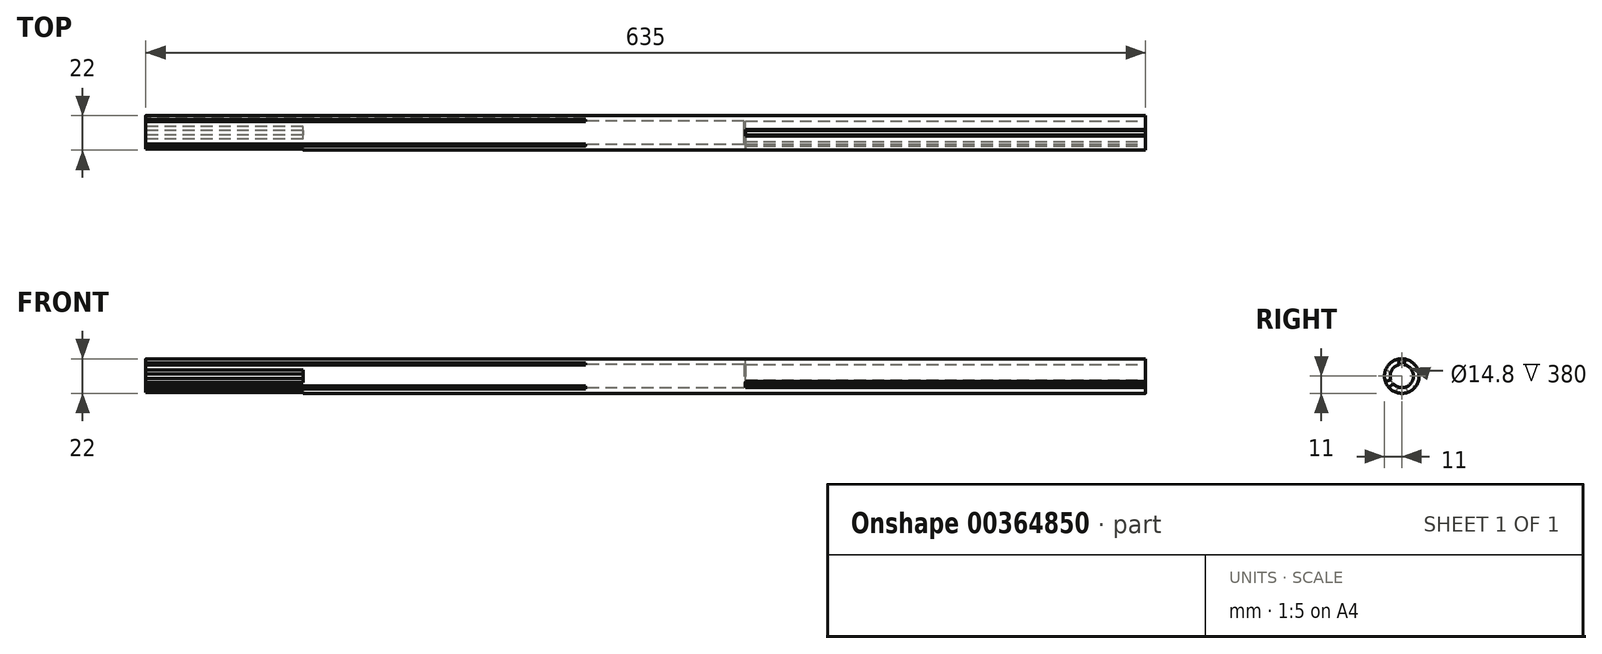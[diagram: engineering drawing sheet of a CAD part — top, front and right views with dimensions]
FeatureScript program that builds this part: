
annotation { "Feature Type Name" : "Feature", "Feature Type Description" : "" }
export const myFeature = defineFeature(function(context is Context, id is Id, definition is map)
    precondition{}
    {
        {
            var Q0;
            Q0=qCreatedBy(makeId("Right.planeOp"),FACE);
            var sketch = newSketch(context, id + "F0", { "sketchPlane" : qUnion([Q0])});
            skCircle(sketch, "E0", {"center": v(0, 0) * mm, "radius": 11 * mm});
            skSolve(sketch);
        }
        {
            var Q0;
            Q0=makeQuery(id+"F0.imprint","IMPRINT",FACE,{"disambiguationData":[TD([[makeQuery(id+"F0.imprint","IMPRINT",EDGE,{"derivedFrom":sQuery(id+"F0.wireOp",EDGE,"E0")}),1.0]])]});
            extrude(context, id + "F1", {"entities" : qUnion([Q0]), "depth" : 635 * mm});
        }
        {
            var Q0;
            Q0=makeQuery(id+"F1.opExtrude","CAP_FACE",FACE,{"disambiguationData":[OSD([sQuery(id+"F0.wireOp",EDGE,"E0")])],"isStart":false});
            var sketch = newSketch(context, id + "F2", { "sketchPlane" : qUnion([Q0])});
            skCircle(sketch, "E1", {"center": v(0, 0) * mm, "radius": 7.39 * mm});
            skLineSegment(sketch, "E2", {"start": v(0, 0) * mm, "end": v(-10.42, -3.54) * mm});
            skLineSegment(sketch, "E3", {"start": v(0, 0) * mm, "end": v(2.15, 10.79) * mm});
            skLineSegment(sketch, "E4", {"start": v(0, 0) * mm, "end": v(8.27, -7.25) * mm});
            skLineSegment(sketch, "E5", {"start": v(-8.27, -7.25) * mm, "end": v(0, 0) * mm});
            skLineSegment(sketch, "E6", {"start": v(0, 0) * mm, "end": v(10.42, -3.54) * mm});
            skLineSegment(sketch, "E7", {"start": v(0, 0) * mm, "end": v(-2.15, 10.79) * mm});
            skLineSegment(sketch, "E8", {"start": v(0, 0) * mm, "end": v(0, 7.39) * mm});
            skSolve(sketch);
        }
        {
            var Q0;
            {var subQ3=sQuery(id+"F2.wireOp",EDGE,"E1");var subQ5=makeQuery(id+"F2.imprint","INTERSECT",VERTEX,{"derivedFrom":[subQ3,sQuery(id+"F2.wireOp",EDGE,"E8")]});Q0=makeQuery(id+"F2.imprint","IMPRINT",FACE,{"disambiguationData":[TD([[makeQuery(id+"F2.imprint","IMPRINT",EDGE,{"disambiguationData":[TD([[subQ5,1.0]])],"derivedFrom":subQ3}),-1.0]])]});}
            var Q1;
            {var subQ0=sQuery(id+"F2.wireOp",EDGE,"E7");var subQ1=sQuery(id+"F2.wireOp",EDGE,"E1");var subQ2=makeQuery(id+"F2.imprint","INTERSECT",VERTEX,{"derivedFrom":[subQ1,subQ0]});Q1=makeQuery(id+"F2.imprint","IMPRINT",FACE,{"disambiguationData":[TD([[makeQuery(id+"F2.imprint","IMPRINT",EDGE,{"disambiguationData":[TD([[subQ2,-1.0]])],"derivedFrom":subQ1}),1.0]])]});}
            var Q2;
            {var subQ0=sQuery(id+"F2.wireOp",EDGE,"E2");var subQ1=sQuery(id+"F2.wireOp",EDGE,"E1");var subQ2=makeQuery(id+"F2.imprint","INTERSECT",VERTEX,{"derivedFrom":[subQ1,subQ0]});Q2=makeQuery(id+"F2.imprint","IMPRINT",FACE,{"disambiguationData":[TD([[makeQuery(id+"F2.imprint","IMPRINT",EDGE,{"disambiguationData":[TD([[subQ2,-1.0]])],"derivedFrom":subQ1}),1.0]])]});}
            var Q3;
            {var subQ0=sQuery(id+"F2.wireOp",EDGE,"E5");var subQ1=sQuery(id+"F2.wireOp",EDGE,"E1");var subQ2=makeQuery(id+"F2.imprint","INTERSECT",VERTEX,{"derivedFrom":[subQ1,subQ0]});Q3=makeQuery(id+"F2.imprint","IMPRINT",FACE,{"disambiguationData":[TD([[makeQuery(id+"F2.imprint","IMPRINT",EDGE,{"disambiguationData":[TD([[subQ2,-1.0]])],"derivedFrom":subQ1}),1.0]])]});}
            var Q4;
            {var subQ0=sQuery(id+"F2.wireOp",EDGE,"E4");var subQ1=sQuery(id+"F2.wireOp",EDGE,"E1");var subQ2=makeQuery(id+"F2.imprint","INTERSECT",VERTEX,{"derivedFrom":[subQ1,subQ0]});Q4=makeQuery(id+"F2.imprint","IMPRINT",FACE,{"disambiguationData":[TD([[makeQuery(id+"F2.imprint","IMPRINT",EDGE,{"disambiguationData":[TD([[subQ2,-1.0]])],"derivedFrom":subQ1}),1.0]])]});}
            var Q5;
            {var subQ0=sQuery(id+"F2.wireOp",EDGE,"E3");var subQ1=sQuery(id+"F2.wireOp",EDGE,"E1");var subQ2=makeQuery(id+"F2.imprint","INTERSECT",VERTEX,{"derivedFrom":[subQ1,subQ0]});Q5=makeQuery(id+"F2.imprint","IMPRINT",FACE,{"disambiguationData":[TD([[makeQuery(id+"F2.imprint","IMPRINT",EDGE,{"disambiguationData":[TD([[subQ2,1.0]])],"derivedFrom":subQ1}),1.0]])]});}
            var Q6;
            {var subQ0=sQuery(id+"F2.wireOp",EDGE,"E8");Q6=makeQuery(id+"F2.imprint","IMPRINT",FACE,{"disambiguationData":[TD([[makeQuery(id+"F2.imprint","IMPRINT",EDGE,{"derivedFrom":subQ0}),-1.0]])]});}
            var Q7;
            {var subQ0=sQuery(id+"F2.wireOp",EDGE,"E8");Q7=makeQuery(id+"F2.imprint","IMPRINT",FACE,{"disambiguationData":[TD([[makeQuery(id+"F2.imprint","IMPRINT",EDGE,{"derivedFrom":subQ0}),1.0]])]});}
            var Q8;
            {var subQ0=sQuery(id+"F2.wireOp",EDGE,"E2");var subQ1=sQuery(id+"F2.wireOp",EDGE,"E1");var subQ2=makeQuery(id+"F2.imprint","INTERSECT",VERTEX,{"derivedFrom":[subQ1,subQ0]});Q8=makeQuery(id+"F2.imprint","IMPRINT",FACE,{"disambiguationData":[TD([[makeQuery(id+"F2.imprint","IMPRINT",EDGE,{"disambiguationData":[TD([[subQ2,-1.0]])],"derivedFrom":subQ1}),-1.0]])]});}
            var Q9;
            {var subQ0=sQuery(id+"F2.wireOp",EDGE,"E4");var subQ1=sQuery(id+"F2.wireOp",EDGE,"E1");var subQ2=makeQuery(id+"F2.imprint","INTERSECT",VERTEX,{"derivedFrom":[subQ1,subQ0]});Q9=makeQuery(id+"F2.imprint","IMPRINT",FACE,{"disambiguationData":[TD([[makeQuery(id+"F2.imprint","IMPRINT",EDGE,{"disambiguationData":[TD([[subQ2,-1.0]])],"derivedFrom":subQ1}),-1.0]])]});}
            extrude(context, id + "F3", {"entities" : qUnion([Q0, Q1, Q2, Q3, Q4, Q5, Q6, Q7, Q8, Q9]), "operationType" : NewBodyOperationType.REMOVE, "oppositeDirection" : true, "depth" : 254 * mm});
        }
        {
            var Q0;
            Q0=makeQuery(id+"F1.opExtrude","CAP_FACE",FACE,{"disambiguationData":[OSD([sQuery(id+"F0.wireOp",EDGE,"E0")])],"isStart":true});
            var sketch = newSketch(context, id + "F4", { "sketchPlane" : qUnion([Q0])});
            skCircle(sketch, "E9", {"center": v(0, 0) * mm, "radius": 7.4 * mm});
            skSolve(sketch);
        }
        {
            var Q0;
            Q0=makeQuery(id+"F4.imprint","IMPRINT",FACE,{"disambiguationData":[TD([[makeQuery(id+"F4.imprint","IMPRINT",EDGE,{"derivedFrom":sQuery(id+"F4.wireOp",EDGE,"E9")}),1.0]])]});
            extrude(context, id + "F5", {"entities" : qUnion([Q0]), "operationType" : NewBodyOperationType.REMOVE, "oppositeDirection" : true, "depth" : 380 * mm});
        }
        {
            var Q0;
            Q0=makeQuery(id+"F1.opExtrude","CAP_FACE",FACE,{"disambiguationData":[OSD([sQuery(id+"F0.wireOp",EDGE,"E0")])],"isStart":true});
            var sketch = newSketch(context, id + "F6", { "sketchPlane" : qUnion([Q0])});
            skLineSegment(sketch, "E10.bottom", {"start": v(7.12, 6.97) * mm, "end": v(9.12, 6.97) * mm});
            skLineSegment(sketch, "E10.top", {"start": v(7.12, 8.97) * mm, "end": v(9.12, 8.97) * mm});
            skLineSegment(sketch, "E10.left", {"start": v(7.12, 6.97) * mm, "end": v(7.12, 8.97) * mm});
            skLineSegment(sketch, "E10.right", {"start": v(9.12, 6.97) * mm, "end": v(9.12, 8.97) * mm});
            skLineSegment(sketch, "E11.bottom", {"start": v(-7.2, 6.97) * mm, "end": v(-9.2, 6.97) * mm});
            skLineSegment(sketch, "E11.top", {"start": v(-7.2, 8.97) * mm, "end": v(-9.2, 8.97) * mm});
            skLineSegment(sketch, "E11.left", {"start": v(-7.2, 6.97) * mm, "end": v(-7.2, 8.97) * mm});
            skLineSegment(sketch, "E11.right", {"start": v(-9.2, 6.97) * mm, "end": v(-9.2, 8.97) * mm});
            skLineSegment(sketch, "E12.bottom", {"start": v(-7.2, -6.27) * mm, "end": v(-9.2, -6.27) * mm});
            skLineSegment(sketch, "E12.top", {"start": v(-7.2, -8.27) * mm, "end": v(-9.2, -8.27) * mm});
            skLineSegment(sketch, "E12.left", {"start": v(-7.2, -6.27) * mm, "end": v(-7.2, -8.27) * mm});
            skLineSegment(sketch, "E12.right", {"start": v(-9.2, -6.27) * mm, "end": v(-9.2, -8.27) * mm});
            skLineSegment(sketch, "E13.bottom", {"start": v(7.12, -6.27) * mm, "end": v(9.12, -6.27) * mm});
            skLineSegment(sketch, "E13.top", {"start": v(7.12, -8.27) * mm, "end": v(9.12, -8.27) * mm});
            skLineSegment(sketch, "E13.left", {"start": v(7.12, -6.27) * mm, "end": v(7.12, -8.27) * mm});
            skLineSegment(sketch, "E13.right", {"start": v(9.12, -6.27) * mm, "end": v(9.12, -8.27) * mm});
            skCircle(sketch, "E14", {"center": v(11, 0) * mm, "radius": 4 * mm});
            skCircle(sketch, "E15", {"center": v(0, 11) * mm, "radius": 4 * mm});
            skCircle(sketch, "E16", {"center": v(-11, 0) * mm, "radius": 4 * mm});
            skCircle(sketch, "E17", {"center": v(0, -11) * mm, "radius": 4 * mm});
            skSolve(sketch);
        }
        {
            var Q0;
            {var subQ0=sQuery(id+"F6.wireOp",EDGE,"E10.left");var subQ1=sQuery(id+"F6.wireOp",EDGE,"E10.bottom");var subQ2=makeQuery(id+"F6.imprint","INTERSECT",VERTEX,{"derivedFrom":[subQ1,subQ0]});Q0=makeQuery(id+"F6.imprint","IMPRINT",FACE,{"disambiguationData":[TD([[makeQuery(id+"F6.imprint","IMPRINT",EDGE,{"disambiguationData":[TD([[subQ2,-1.0]])],"derivedFrom":subQ1}),1.0]])]});}
            var Q1;
            {var subQ0=sQuery(id+"F6.wireOp",EDGE,"E12.left");Q1=makeQuery(id+"F6.imprint","IMPRINT",FACE,{"disambiguationData":[TD([[makeQuery(id+"F6.imprint","IMPRINT",EDGE,{"derivedFrom":subQ0}),-1.0]])]});}
            var Q2;
            {var subQ0=sQuery(id+"F6.wireOp",EDGE,"E13.left");Q2=makeQuery(id+"F6.imprint","IMPRINT",FACE,{"disambiguationData":[TD([[makeQuery(id+"F6.imprint","IMPRINT",EDGE,{"derivedFrom":subQ0}),1.0]])]});}
            var Q3;
            {var subQ0=sQuery(id+"F6.wireOp",EDGE,"E11.left");var subQ1=sQuery(id+"F6.wireOp",EDGE,"E11.bottom");var subQ2=makeQuery(id+"F6.imprint","INTERSECT",VERTEX,{"derivedFrom":[subQ1,subQ0]});Q3=makeQuery(id+"F6.imprint","IMPRINT",FACE,{"disambiguationData":[TD([[makeQuery(id+"F6.imprint","IMPRINT",EDGE,{"disambiguationData":[TD([[subQ2,-1.0]])],"derivedFrom":subQ1}),-1.0]])]});}
            extrude(context, id + "F7", {"entities" : qUnion([Q0, Q1, Q2, Q3]), "operationType" : NewBodyOperationType.REMOVE, "oppositeDirection" : true, "depth" : 279.4 * mm});
        }
        {
            var Q0;
            {var subQ0=sQuery(id+"F6.wireOp",EDGE,"E14");var subQ1=makeQuery(id+"F1.opExtrude","CAP_EDGE",EDGE,{"disambiguationData":[OSD([sQuery(id+"F0.wireOp",EDGE,"E0")])],"isStart":true});var subQ2=makeQuery(id+"F6.imprint","INTERSECT",VERTEX,{"disambiguationData":[OD(0.0)],"derivedFrom":[subQ1,subQ0]});Q0=makeQuery(id+"F6.imprint","IMPRINT",FACE,{"disambiguationData":[TD([[makeQuery(id+"F6.imprint","IMPRINT",EDGE,{"disambiguationData":[TD([[subQ2,-1.0]])],"derivedFrom":subQ0}),1.0]])]});}
            var Q1;
            {var subQ0=sQuery(id+"F6.wireOp",EDGE,"E17");var subQ1=makeQuery(id+"F1.opExtrude","CAP_EDGE",EDGE,{"disambiguationData":[OSD([sQuery(id+"F0.wireOp",EDGE,"E0")])],"isStart":true});var subQ2=makeQuery(id+"F6.imprint","INTERSECT",VERTEX,{"disambiguationData":[OD(0.0)],"derivedFrom":[subQ1,subQ0]});Q1=makeQuery(id+"F6.imprint","IMPRINT",FACE,{"disambiguationData":[TD([[makeQuery(id+"F6.imprint","IMPRINT",EDGE,{"disambiguationData":[TD([[subQ2,1.0]])],"derivedFrom":subQ0}),1.0]])]});}
            var Q2;
            {var subQ0=sQuery(id+"F6.wireOp",EDGE,"E16");var subQ1=makeQuery(id+"F1.opExtrude","CAP_EDGE",EDGE,{"disambiguationData":[OSD([sQuery(id+"F0.wireOp",EDGE,"E0")])],"isStart":true});var subQ2=makeQuery(id+"F6.imprint","INTERSECT",VERTEX,{"disambiguationData":[OD(0.0)],"derivedFrom":[subQ1,subQ0]});Q2=makeQuery(id+"F6.imprint","IMPRINT",FACE,{"disambiguationData":[TD([[makeQuery(id+"F6.imprint","IMPRINT",EDGE,{"disambiguationData":[TD([[subQ2,1.0]])],"derivedFrom":subQ0}),1.0]])]});}
            var Q3;
            {var subQ0=sQuery(id+"F6.wireOp",EDGE,"E15");var subQ1=makeQuery(id+"F1.opExtrude","CAP_EDGE",EDGE,{"disambiguationData":[OSD([sQuery(id+"F0.wireOp",EDGE,"E0")])],"isStart":true});var subQ2=makeQuery(id+"F6.imprint","INTERSECT",VERTEX,{"disambiguationData":[OD(0.0)],"derivedFrom":[subQ1,subQ0]});Q3=makeQuery(id+"F6.imprint","IMPRINT",FACE,{"disambiguationData":[TD([[makeQuery(id+"F6.imprint","IMPRINT",EDGE,{"disambiguationData":[TD([[subQ2,1.0]])],"derivedFrom":subQ0}),1.0]])]});}
            extrude(context, id + "F8", {"entities" : qUnion([Q0, Q1, Q2, Q3]), "operationType" : NewBodyOperationType.REMOVE, "oppositeDirection" : true, "depth" : 100 * mm});
        }
    });
